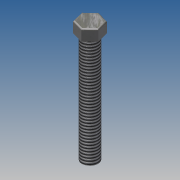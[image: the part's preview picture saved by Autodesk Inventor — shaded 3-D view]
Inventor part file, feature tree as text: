
AUTODESK INVENTOR PART (.ipt)
format: ipt  version: 2014 SP1 (Build 180222100, 222)  size: 96,768 bytes
history: native  units: in
note: dims shown in document units (in); Inventor stores cm internally (conversion verified against a paired STEP export)
features: extrude x2, sketch x2, fillet x1, thread x1
ambient origin geometry x8: Origin, YZ Plane, XZ Plane, XY Plane, X Axis, Y Axis, Z Axis, Center Point
bodies: Solid1 (feature_tree)
feature tree (6):
  extrude  "Extrusion1"  Depth=0.03in
  fillet  "Fillet1"  Radius=0.366in
  extrude  "Extrusion2"  Depth=2.5in TaperAngle=0.0deg
  thread  "Thread1"  [1 undecoded]
  sketch  "Sketch1"  dims[d0=0.25in d1=0.0in d2=0.03in d3=0.366in]
  sketch  "Sketch2"  dims[d4=2.5in d5=0.0in d6=1.0in d7=0.0in]
note: 1 required parameter value undecoded (feature->parameter linkage not recoverable at this tier; creation-order binding heuristic only, values carry confidence <= 0.55)
